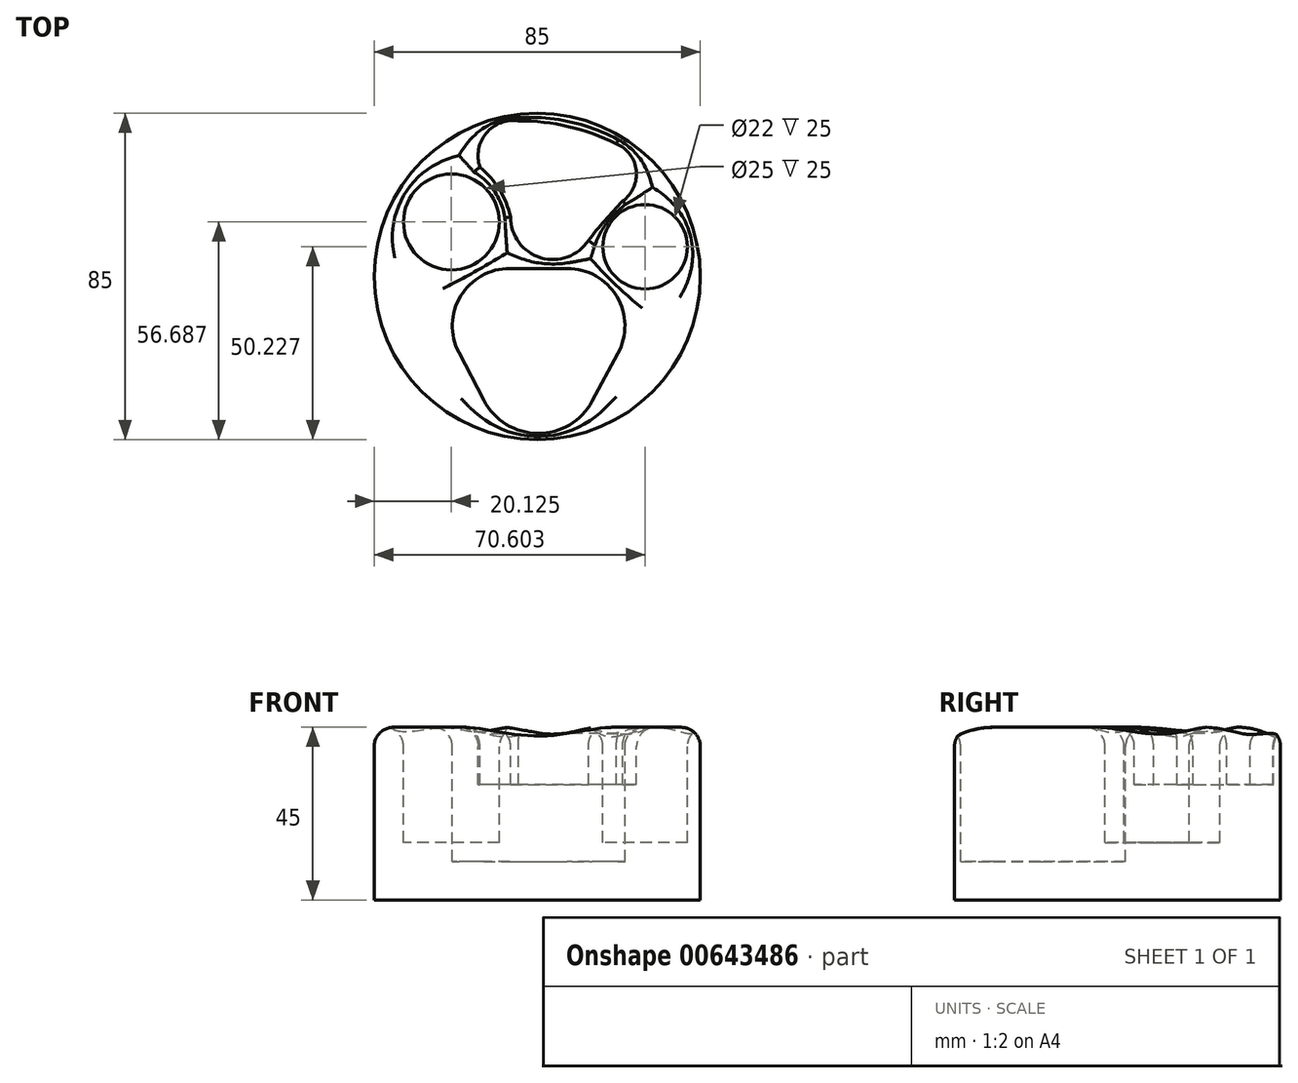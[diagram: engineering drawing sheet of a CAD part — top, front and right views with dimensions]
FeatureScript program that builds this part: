
annotation { "Feature Type Name" : "Feature", "Feature Type Description" : "" }
export const myFeature = defineFeature(function(context is Context, id is Id, definition is map)
    precondition{}
    {
        {
            var Q0;
            Q0=qCreatedBy(makeId("Top.planeOp"),FACE);
            var sketch = newSketch(context, id + "F0", { "sketchPlane" : qUnion([Q0])});
            skCircle(sketch, "E0", {"center": v(0, 0) * mm, "radius": 42.5 * mm});
            skSolve(sketch);
        }
        {
            var Q0;
            Q0=makeQuery(id+"F0.imprint","IMPRINT",FACE,{"disambiguationData":[TD([[makeQuery(id+"F0.imprint","IMPRINT",EDGE,{"derivedFrom":sQuery(id+"F0.wireOp",EDGE,"E0")}),1.0]])]});
            extrude(context, id + "F1", {"entities" : qUnion([Q0]), "depth" : 45 * mm, "offsetDistance" : 25 * mm});
        }
        {
            var Q0;
            Q0=makeQuery(id+"F1.opExtrude","CAP_FACE",FACE,{"disambiguationData":[OSD([sQuery(id+"F0.wireOp",EDGE,"E0")])],"isStart":false});
            var sketch = newSketch(context, id + "F2", { "sketchPlane" : qUnion([Q0])});
            skLineSegment(sketch, "E1.0", {"start": v(21.05, -20.03) * mm, "end": v(14.32, -32.5) * mm});
            skLineSegment(sketch, "E1.1", {"start": v(-13.94, -32.3) * mm, "end": v(-20.45, -19.84) * mm});
            skLineSegment(sketch, "E1.2", {"start": v(-7.15, 2.1) * mm, "end": v(7.85, 2.1) * mm});
            skPoint(sketch, "E2.visualSharp", {"position": v(-31.89, 2.1) * mm});
            skArc(sketch, "E2.filletArc", {"start": v(-7.15, 2.1) * mm, "mid": v(-19.97, -5.13) * mm, "end": v(-20.45, -19.84) * mm});
            skPoint(sketch, "E3.visualSharp", {"position": v(33, 2.1) * mm});
            skArc(sketch, "E3.filletArc", {"start": v(21.05, -20.03) * mm, "mid": v(20.74, -5.22) * mm, "end": v(7.85, 2.1) * mm});
            skPoint(sketch, "E4.visualSharp", {"position": v(0, -59.04) * mm});
            skArc(sketch, "E4.filletArc", {"start": v(-13.94, -32.3) * mm, "mid": v(0.13, -40.9) * mm, "end": v(14.32, -32.5) * mm});
            skSolve(sketch);
        }
        {
            var Q0;
            Q0=makeQuery(id+"F2.imprint","IMPRINT",FACE,{"disambiguationData":[TD([[makeQuery(id+"F2.imprint","IMPRINT",EDGE,{"derivedFrom":sQuery(id+"F2.wireOp",EDGE,"E1.0")}),-1.0]])]});
            extrude(context, id + "F3", {"entities" : qUnion([Q0]), "operationType" : NewBodyOperationType.REMOVE, "oppositeDirection" : true, "depth" : 35 * mm, "offsetDistance" : 25 * mm});
        }
        {
            var Q0;
            Q0=makeQuery(id+"F1.opExtrude","CAP_FACE",FACE,{"disambiguationData":[OSD([sQuery(id+"F0.wireOp",EDGE,"E0")])],"isStart":false});
            var sketch = newSketch(context, id + "F4", { "sketchPlane" : qUnion([Q0])});
            skCircle(sketch, "E5", {"center": v(-22.38, 14.19) * mm, "radius": 12.5 * mm});
            skCircle(sketch, "E6", {"center": v(28.1, 7.73) * mm, "radius": 11 * mm});
            skSolve(sketch);
        }
        {
            var Q0;
            Q0=makeQuery(id+"F4.imprint","IMPRINT",FACE,{"disambiguationData":[TD([[makeQuery(id+"F4.imprint","IMPRINT",EDGE,{"derivedFrom":sQuery(id+"F4.wireOp",EDGE,"E5")}),1.0]])]});
            var Q1;
            Q1=makeQuery(id+"F4.imprint","IMPRINT",FACE,{"disambiguationData":[TD([[makeQuery(id+"F4.imprint","IMPRINT",EDGE,{"derivedFrom":sQuery(id+"F4.wireOp",EDGE,"E6")}),1.0]])]});
            extrude(context, id + "F5", {"entities" : qUnion([Q0, Q1]), "operationType" : NewBodyOperationType.REMOVE, "oppositeDirection" : true, "depth" : 30 * mm, "offsetDistance" : 25 * mm});
        }
        {
            var Q0;
            Q0=makeQuery(id+"F1.opExtrude","CAP_FACE",FACE,{"disambiguationData":[OSD([sQuery(id+"F0.wireOp",EDGE,"E0")])],"isStart":false});
            var sketch = newSketch(context, id + "F6", { "sketchPlane" : qUnion([Q0])});
            skArc(sketch, "E7", {"start": v(-6.93, 15.5) * mm, "mid": v(0.91, 4.87) * mm, "end": v(13.33, 9.4) * mm});
            skArc(sketch, "E8", {"start": v(-4.88, 40.58) * mm, "mid": v(-13.3, 37.34) * mm, "end": v(-14.95, 28.46) * mm});
            skArc(sketch, "E9", {"start": v(22.26, 19.65) * mm, "mid": v(25.81, 27.6) * mm, "end": v(20.63, 34.6) * mm});
            skArc(sketch, "E10", {"start": v(22.26, 19.65) * mm, "mid": v(17.67, 14.62) * mm, "end": v(13.33, 9.4) * mm});
            skArc(sketch, "E11", {"start": v(-6.93, 15.5) * mm, "mid": v(-9.89, 22.63) * mm, "end": v(-14.95, 28.46) * mm});
            skArc(sketch, "E12", {"start": v(20.63, 34.6) * mm, "mid": v(8.22, 39.05) * mm, "end": v(-4.88, 40.58) * mm});
            skSolve(sketch);
        }
        {
            var Q0;
            Q0=makeQuery(id+"F6.imprint","IMPRINT",FACE,{"disambiguationData":[TD([[makeQuery(id+"F6.imprint","IMPRINT",EDGE,{"derivedFrom":sQuery(id+"F6.wireOp",EDGE,"E7")}),1.0]])]});
            extrude(context, id + "F7", {"entities" : qUnion([Q0]), "operationType" : NewBodyOperationType.REMOVE, "oppositeDirection" : true, "depth" : 15 * mm, "offsetDistance" : 25 * mm});
        }
        {
            var Q0;
            Q0=makeQuery(id+"F1.opExtrude","CAP_EDGE",EDGE,{"disambiguationData":[OSD([sQuery(id+"F0.wireOp",EDGE,"E0")])],"isStart":false});
            var Q1;
            Q1=makeQuery(id+"F1.opExtrude","CAP_FACE",FACE,{"disambiguationData":[OSD([sQuery(id+"F0.wireOp",EDGE,"E0")])],"isStart":false});
            fillet(context, id + "F8", {"entities" : qUnion([Q0, Q1]), "radius" : 5 * mm, "tangentPropagation" : true, "allowEdgeOverflow" : false});
        }
    });
